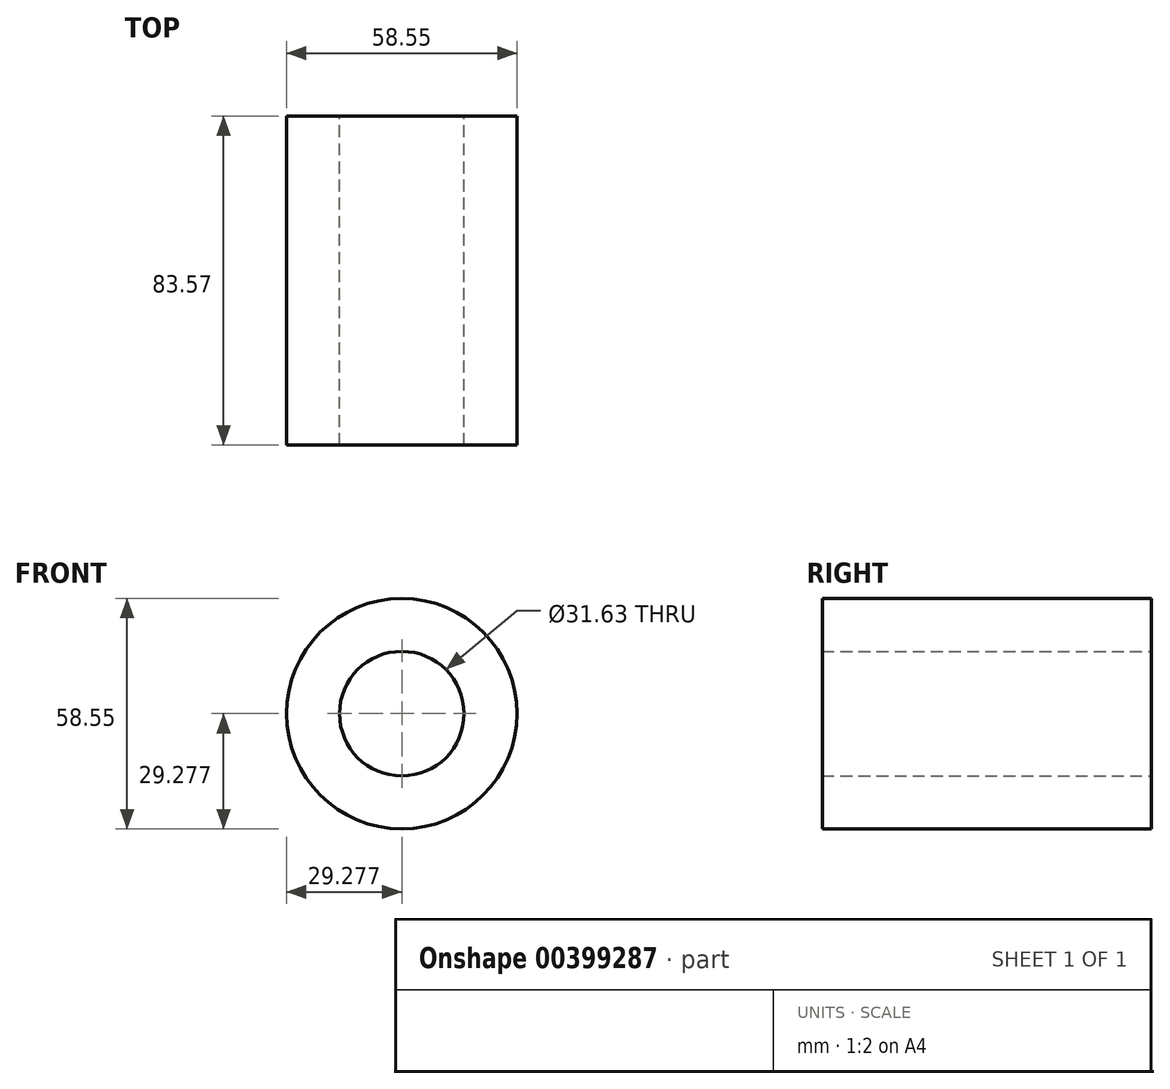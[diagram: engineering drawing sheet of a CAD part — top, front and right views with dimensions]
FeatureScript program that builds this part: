
annotation { "Feature Type Name" : "Feature", "Feature Type Description" : "" }
export const myFeature = defineFeature(function(context is Context, id is Id, definition is map)
    precondition{}
    {
        {
            var Q0;
            Q0=qCreatedBy(makeId("Front.planeOp"),FACE);
            var sketch = newSketch(context, id + "F0", { "sketchPlane" : qUnion([Q0])});
            skCircle(sketch, "E0", {"center": v(-11.87, 30.7) * mm, "radius": 15.82 * mm});
            skCircle(sketch, "E1", {"center": v(-11.87, 30.7) * mm, "radius": 29.27 * mm});
            skSolve(sketch);
        }
        {
            var Q0;
            Q0 = qSketchRegion(id + "F0", true);
            extrude(context, id + "F1", {"entities" : qUnion([Q0]), "depth" : 83.57 * mm});
        }
    });
